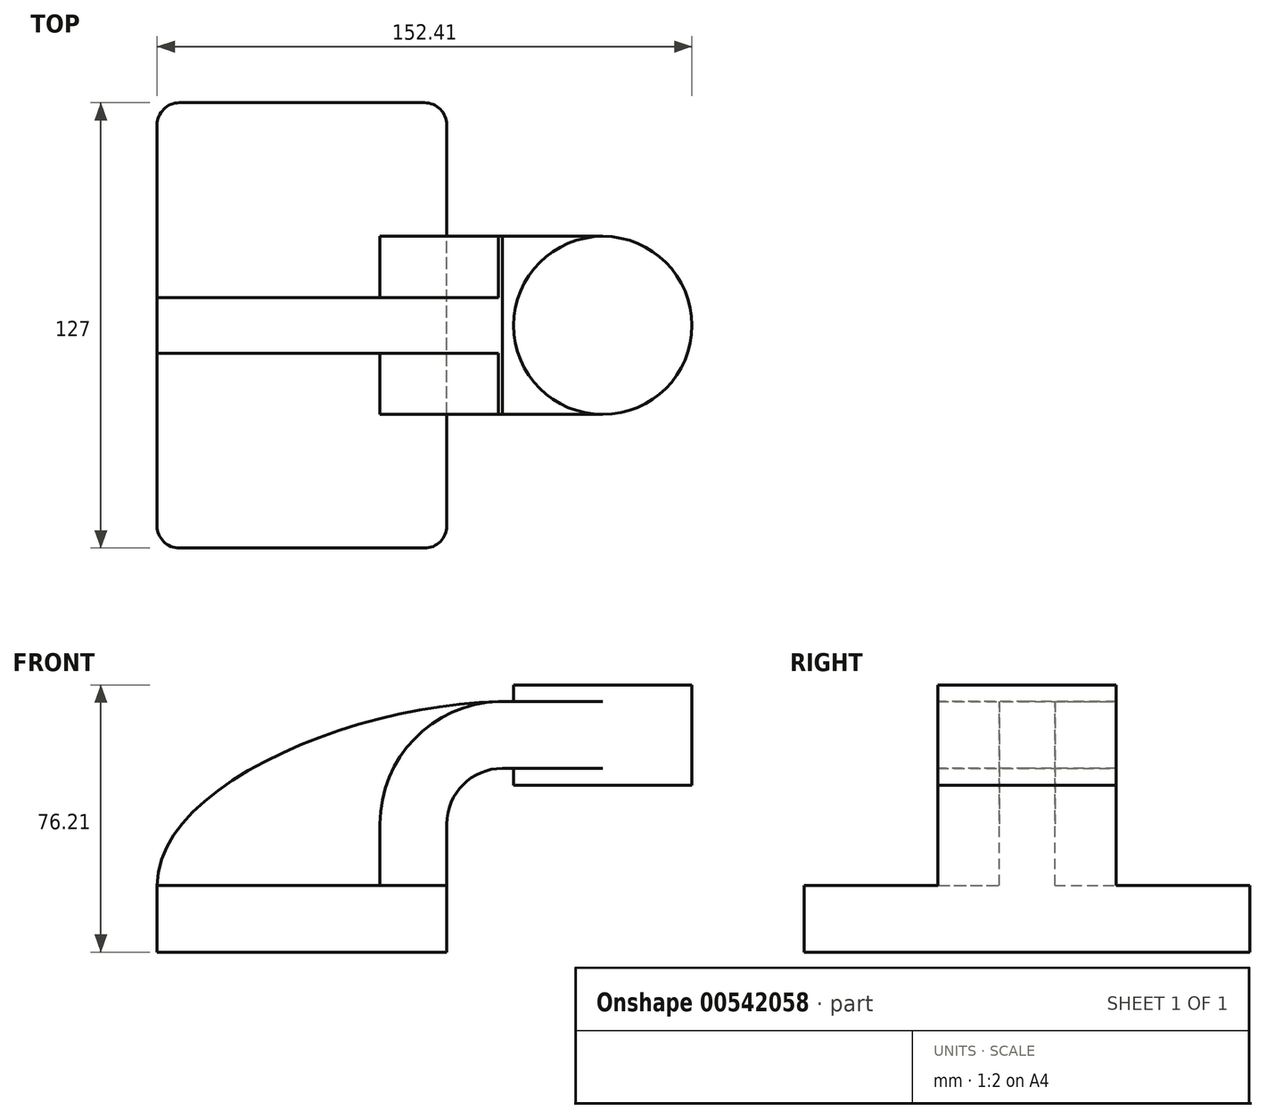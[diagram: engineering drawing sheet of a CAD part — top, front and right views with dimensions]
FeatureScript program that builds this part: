
annotation { "Feature Type Name" : "Feature", "Feature Type Description" : "" }
export const myFeature = defineFeature(function(context is Context, id is Id, definition is map)
    precondition{}
    {
        {
            var Q0;
            Q0=qCreatedBy(makeId("Front.planeOp"),FACE);
            var sketch = newSketch(context, id + "F0", { "sketchPlane" : qUnion([Q0])});
            skLineSegment(sketch, "E0.bottom", {"start": v(41.28, -9.52) * mm, "end": v(-41.28, -9.52) * mm});
            skLineSegment(sketch, "E0.top", {"start": v(41.28, 9.53) * mm, "end": v(-41.28, 9.53) * mm});
            skLineSegment(sketch, "E0.left", {"start": v(41.28, -9.52) * mm, "end": v(41.28, 9.53) * mm});
            skLineSegment(sketch, "E0.right", {"start": v(-41.28, -9.52) * mm, "end": v(-41.28, 9.53) * mm});
            skPoint(sketch, "E0.middle", {"position": v(0, 0) * mm});
            skLineSegment(sketch, "E1.bottom", {"start": v(60.33, 38.1) * mm, "end": v(111.12, 38.1) * mm});
            skLineSegment(sketch, "E1.top", {"start": v(60.33, 66.68) * mm, "end": v(111.12, 66.68) * mm});
            skLineSegment(sketch, "E1.left", {"start": v(60.33, 38.1) * mm, "end": v(60.33, 66.68) * mm});
            skLineSegment(sketch, "E1.right", {"start": v(111.12, 38.1) * mm, "end": v(111.12, 66.68) * mm});
            skPoint(sketch, "E1.middle", {"position": v(85.72, 52.39) * mm});
            skLineSegment(sketch, "E2", {"start": v(41.28, 9.53) * mm, "end": v(41.28, 27) * mm});
            skArc(sketch, "E3", {"start": v(41.27, 27) * mm, "mid": v(45.92, 38.23) * mm, "end": v(57.15, 42.88) * mm});
            skLineSegment(sketch, "E4", {"start": v(57.15, 42.88) * mm, "end": v(85.73, 42.88) * mm});
            skLineSegment(sketch, "E5.0", {"start": v(57.15, 61.93) * mm, "end": v(85.73, 61.93) * mm});
            skArc(sketch, "E5.1", {"start": v(22.23, 27) * mm, "mid": v(32.45, 51.7) * mm, "end": v(57.15, 61.93) * mm});
            skLineSegment(sketch, "E5.2", {"start": v(22.22, 9.53) * mm, "end": v(22.22, 27) * mm});
            skLineSegment(sketch, "E6", {"start": v(85.73, 38.1) * mm, "end": v(85.73, 66.68) * mm});
            skFitSpline(sketch, "E7", {"points": [v(-41.28, 9.52) * mm, v(57.15, 61.93) * mm], "startDerivative": vector(0, 86.1) * mm, "endDerivative": vector(124.49, 1.45) * mm});
            skSolve(sketch);
        }
        {
            var Q0;
            Q0=makeQuery(id+"F0.imprint","IMPRINT",FACE,{"disambiguationData":[TD([[makeQuery(id+"F0.imprint","IMPRINT",EDGE,{"derivedFrom":sQuery(id+"F0.wireOp",EDGE,"E0.bottom")}),-1.0]])]});
            extrude(context, id + "F1", {"entities" : qUnion([Q0]), "endBound" : BoundingType.SYMMETRIC, "depth" : 127 * mm, "offsetDistance" : 25.4 * mm});
        }
        {
            var Q0;
            {var subQ1=sQuery(id+"F0.wireOp",EDGE,"E2");Q0=makeQuery(id+"F0.imprint","IMPRINT",FACE,{"disambiguationData":[TD([[makeQuery(id+"F0.imprint","IMPRINT",EDGE,{"derivedFrom":subQ1}),1.0]])]});}
            var Q1;
            {var subQ0=sQuery(id+"F0.wireOp",EDGE,"E4");var subQ1=sQuery(id+"F0.wireOp",EDGE,"E1.left");var subQ2=makeQuery(id+"F0.imprint","INTERSECT",VERTEX,{"derivedFrom":[subQ1,subQ0]});Q1=makeQuery(id+"F0.imprint","IMPRINT",FACE,{"disambiguationData":[TD([[makeQuery(id+"F0.imprint","IMPRINT",EDGE,{"disambiguationData":[TD([[subQ2,-1.0]])],"derivedFrom":subQ1}),-1.0]])]});}
            extrude(context, id + "F2", {"entities" : qUnion([Q0, Q1]), "operationType" : NewBodyOperationType.ADD, "endBound" : BoundingType.SYMMETRIC, "depth" : 50.8 * mm, "offsetDistance" : 25.4 * mm});
        }
        {
            var Q0;
            {var subQ3=sQuery(id+"F0.wireOp",EDGE,"E5.2");Q0=makeQuery(id+"F0.imprint","IMPRINT",FACE,{"disambiguationData":[TD([[makeQuery(id+"F0.imprint","IMPRINT",EDGE,{"derivedFrom":subQ3}),1.0]])]});}
            extrude(context, id + "F3", {"entities" : qUnion([Q0]), "operationType" : NewBodyOperationType.ADD, "endBound" : BoundingType.SYMMETRIC, "depth" : 15.88 * mm, "offsetDistance" : 25.4 * mm});
        }
        {
            var Q0;
            {var subQ4=sQuery(id+"F0.wireOp",EDGE,"E1.right");Q0=makeQuery(id+"F0.imprint","IMPRINT",FACE,{"disambiguationData":[TD([[makeQuery(id+"F0.imprint","IMPRINT",EDGE,{"derivedFrom":subQ4}),1.0]])]});}
            var Q1;
            Q1=sQuery(id+"F0.wireOp",EDGE,"E6");
            revolve(context, id + "F4", {"operationType" : NewBodyOperationType.ADD, "entities" : qUnion([Q0]), "axis" : qUnion([Q1]), "revolveType" : RevolveType.FULL});
        }
        {
            var Q0;
            Q0=makeQuery(id+"F1.opExtrude","CAP_EDGE",EDGE,{"disambiguationData":[OSD([sQuery(id+"F0.wireOp",EDGE,"E0.right")])],"isStart":false});
            var Q1;
            Q1=makeQuery(id+"F1.opExtrude","CAP_EDGE",EDGE,{"disambiguationData":[OSD([sQuery(id+"F0.wireOp",EDGE,"E0.left")])],"isStart":false});
            var Q2;
            Q2=makeQuery(id+"F1.opExtrude","CAP_EDGE",EDGE,{"disambiguationData":[OSD([sQuery(id+"F0.wireOp",EDGE,"E0.left")])],"isStart":true});
            var Q3;
            Q3=makeQuery(id+"F1.opExtrude","CAP_EDGE",EDGE,{"disambiguationData":[OSD([sQuery(id+"F0.wireOp",EDGE,"E0.right")])],"isStart":true});
            fillet(context, id + "F5", {"entities" : qUnion([Q0, Q1, Q2, Q3]), "radius" : 6.35 * mm, "tangentPropagation" : true, "allowEdgeOverflow" : false});
        }
    });
